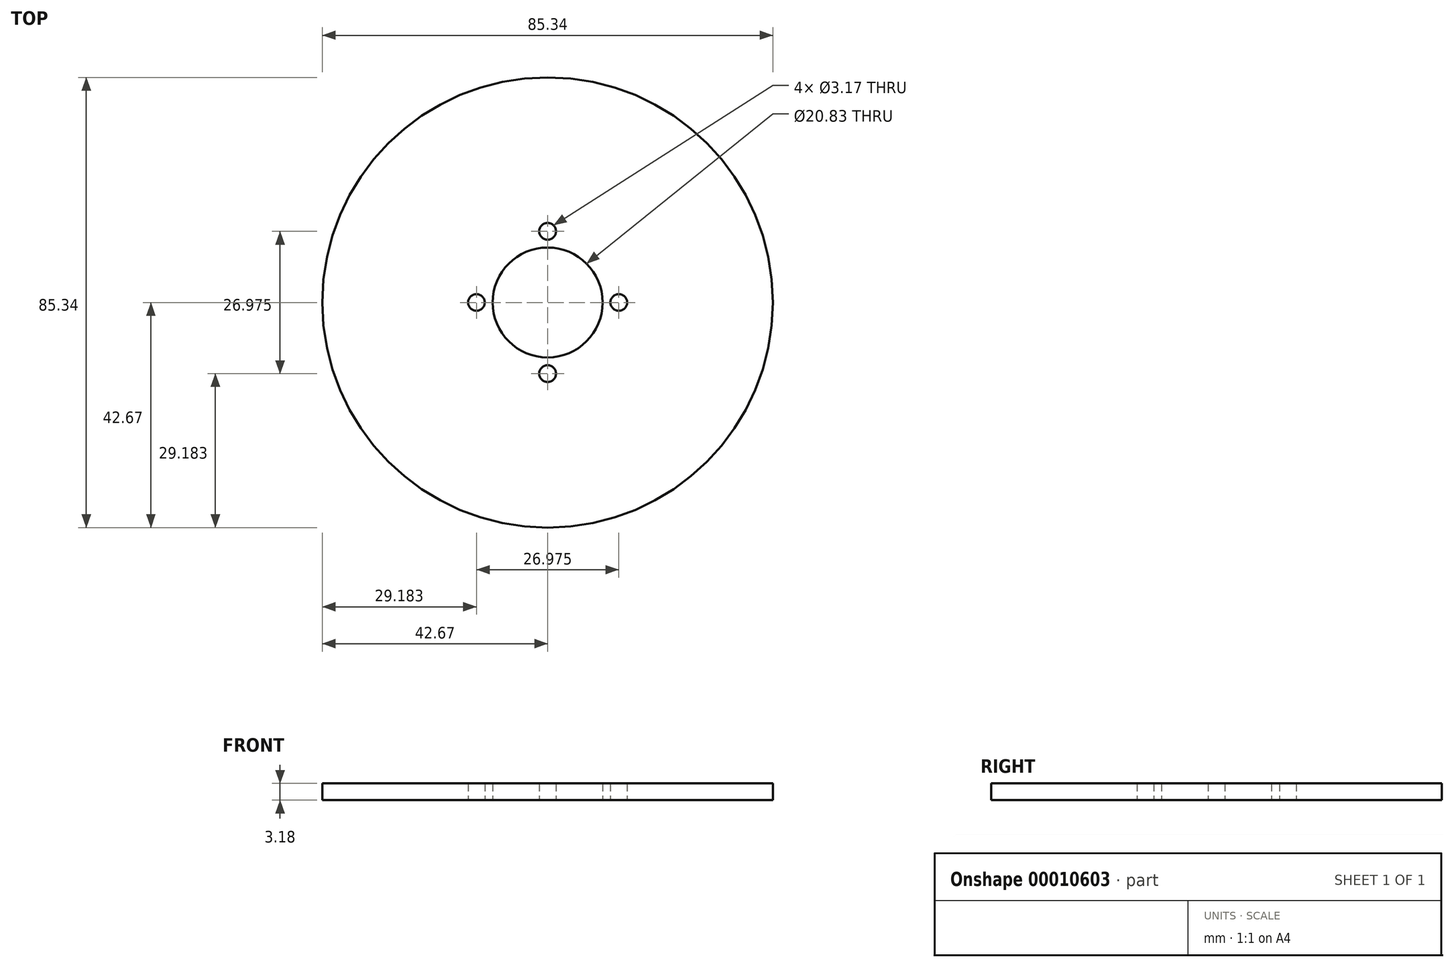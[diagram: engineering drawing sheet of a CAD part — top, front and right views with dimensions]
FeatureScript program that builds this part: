
annotation { "Feature Type Name" : "Feature", "Feature Type Description" : "" }
export const myFeature = defineFeature(function(context is Context, id is Id, definition is map)
    precondition{}
    {
        {
            var Q0;
            Q0=qCreatedBy(makeId("Top.planeOp"),FACE);
            var sketch = newSketch(context, id + "F0", { "sketchPlane" : qUnion([Q0])});
            skCircle(sketch, "E0", {"center": v(0, 0) * mm, "radius": 42.67 * mm});
            skCircle(sketch, "E1", {"center": v(0, 0) * mm, "radius": 10.41 * mm});
            skLineSegment(sketch, "E2", {"start": v(0, 42.67) * mm, "end": v(0, -42.67) * mm, "construction": true});
            skLineSegment(sketch, "E3", {"start": v(-42.67, 0) * mm, "end": v(42.67, 0) * mm, "construction": true});
            skCircle(sketch, "E4", {"center": v(0, 13.49) * mm, "radius": 1.59 * mm});
            skCircle(sketch, "E5", {"center": v(-13.49, 0) * mm, "radius": 1.59 * mm});
            skCircle(sketch, "E6.0.MirrorC", {"center": v(13.49, 0) * mm, "radius": 1.59 * mm});
            skCircle(sketch, "E7.0.MirrorC", {"center": v(0, -13.49) * mm, "radius": 1.59 * mm});
            skSolve(sketch);
        }
        {
            var Q0;
            Q0=qSketchRegion(id+"F0",true);
            extrude(context, id + "F1", {"entities" : qUnion([Q0]), "depth" : 3.17 * mm});
        }
    });
